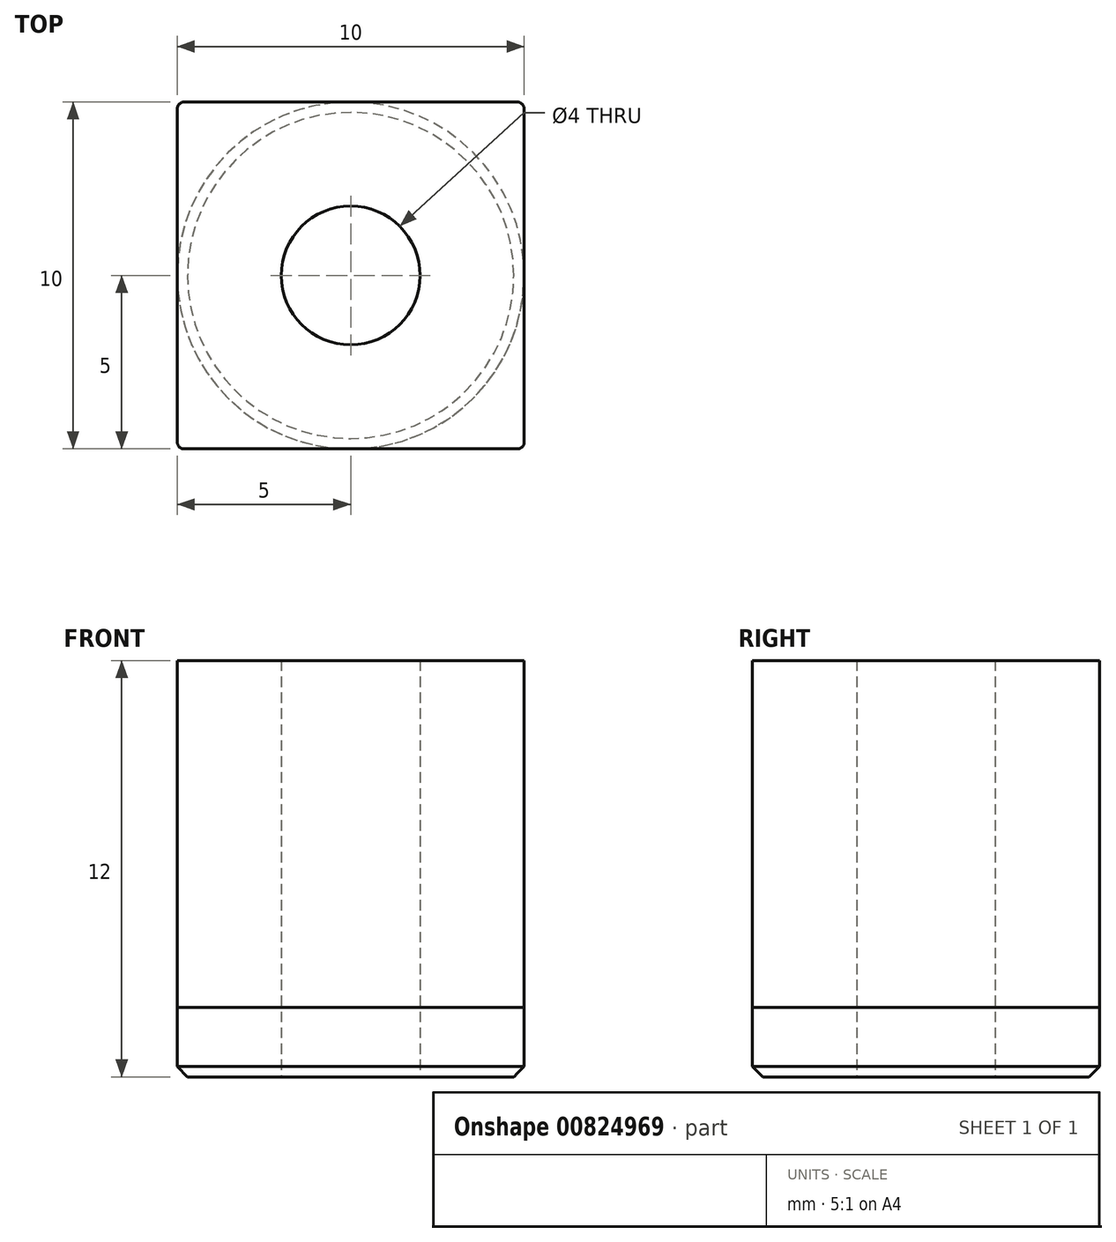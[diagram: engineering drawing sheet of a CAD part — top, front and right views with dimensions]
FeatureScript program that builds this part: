
annotation { "Feature Type Name" : "Feature", "Feature Type Description" : "" }
export const myFeature = defineFeature(function(context is Context, id is Id, definition is map)
    precondition{}
    {
        {
            var Q0;
            Q0=qCreatedBy(makeId("Top.planeOp"),FACE);
            var sketch = newSketch(context, id + "F0", { "sketchPlane" : qUnion([Q0])});
            skLineSegment(sketch, "E0.bottom", {"start": v(5, 5) * mm, "end": v(-5, 5) * mm});
            skLineSegment(sketch, "E0.top", {"start": v(5, -5) * mm, "end": v(-5, -5) * mm});
            skLineSegment(sketch, "E0.left", {"start": v(5, 5) * mm, "end": v(5, -5) * mm});
            skLineSegment(sketch, "E0.right", {"start": v(-5, 5) * mm, "end": v(-5, -5) * mm});
            skPoint(sketch, "E0.middle", {"position": v(0, 0) * mm});
            skCircle(sketch, "E1", {"center": v(0, 0) * mm, "radius": 2 * mm});
            skCircle(sketch, "E2", {"center": v(0, 0) * mm, "radius": 5 * mm});
            skSolve(sketch);
        }
        {
            var Q0;
            Q0=makeQuery(id+"F0.imprint","IMPRINT",FACE,{"disambiguationData":[TD([[makeQuery(id+"F0.imprint","IMPRINT",EDGE,{"derivedFrom":sQuery(id+"F0.wireOp",EDGE,"E0.bottom")}),1.0]])]});
            var Q1;
            Q1=makeQuery(id+"F0.imprint","IMPRINT",FACE,{"disambiguationData":[TD([[makeQuery(id+"F0.imprint","IMPRINT",EDGE,{"derivedFrom":sQuery(id+"F0.wireOp",EDGE,"E1")}),-1.0]])]});
            var Q2;
            {var subQ0=sQuery(id+"F0.wireOp",EDGE,"E0.left");var subQ1=sQuery(id+"F0.wireOp",EDGE,"E0.top");var subQ2=makeQuery(id+"F0.imprint","INTERSECT",VERTEX,{"derivedFrom":[subQ1,subQ0]});Q2=makeQuery(id+"F0.imprint","IMPRINT",FACE,{"disambiguationData":[TD([[makeQuery(id+"F0.imprint","IMPRINT",EDGE,{"disambiguationData":[TD([[subQ2,-1.0]])],"derivedFrom":subQ1}),-1.0]])]});}
            var Q3;
            {var subQ0=sQuery(id+"F0.wireOp",EDGE,"E0.right");var subQ1=sQuery(id+"F0.wireOp",EDGE,"E0.top");var subQ2=makeQuery(id+"F0.imprint","INTERSECT",VERTEX,{"derivedFrom":[subQ1,subQ0]});Q3=makeQuery(id+"F0.imprint","IMPRINT",FACE,{"disambiguationData":[TD([[makeQuery(id+"F0.imprint","IMPRINT",EDGE,{"disambiguationData":[TD([[subQ2,1.0]])],"derivedFrom":subQ1}),-1.0]])]});}
            extrude(context, id + "F1", {"entities" : qUnion([Q0, Q1, Q2, Q3]), "depth" : 10 * mm, "offsetDistance" : 25 * mm});
        }
        {
            var Q0;
            Q0=makeQuery(id+"F0.imprint","IMPRINT",FACE,{"disambiguationData":[TD([[makeQuery(id+"F0.imprint","IMPRINT",EDGE,{"derivedFrom":sQuery(id+"F0.wireOp",EDGE,"E1")}),-1.0]])]});
            extrude(context, id + "F2", {"entities" : qUnion([Q0]), "operationType" : NewBodyOperationType.ADD, "oppositeDirection" : true, "depth" : 2 * mm, "offsetDistance" : 25 * mm});
        }
        {
            var Q0;
            Q0=makeQuery(id+"F2.opExtrude","CAP_EDGE",EDGE,{"disambiguationData":[OSD([sQuery(id+"F0.wireOp",EDGE,"E2")])],"isStart":false});
            chamfer(context, id + "F3", {"entities" : qUnion([Q0]), "width" : 0.3 * mm, "tangentPropagation" : true});
        }
        {
            var Q0;
            Q0=makeQuery(id+"F1.opExtrude","SWEPT_EDGE",EDGE,{"disambiguationData":[OSD([sQuery(id+"F0.wireOp",EDGE,"E0.bottom"),sQuery(id+"F0.wireOp",EDGE,"E0.left")])]});
            var Q1;
            Q1=makeQuery(id+"F1.opExtrude","SWEPT_EDGE",EDGE,{"disambiguationData":[OSD([sQuery(id+"F0.wireOp",EDGE,"E0.top"),sQuery(id+"F0.wireOp",EDGE,"E0.left")])]});
            var Q2;
            Q2=makeQuery(id+"F1.opExtrude","SWEPT_EDGE",EDGE,{"disambiguationData":[OSD([sQuery(id+"F0.wireOp",EDGE,"E0.bottom"),sQuery(id+"F0.wireOp",EDGE,"E0.right")])]});
            var Q3;
            Q3=makeQuery(id+"F1.opExtrude","SWEPT_EDGE",EDGE,{"disambiguationData":[OSD([sQuery(id+"F0.wireOp",EDGE,"E0.top"),sQuery(id+"F0.wireOp",EDGE,"E0.right")])]});
            fillet(context, id + "F4", {"entities" : qUnion([Q0, Q1, Q2, Q3]), "radius" : 0.2 * mm, "tangentPropagation" : true, "allowEdgeOverflow" : false});
        }
    });
